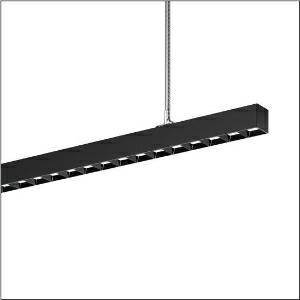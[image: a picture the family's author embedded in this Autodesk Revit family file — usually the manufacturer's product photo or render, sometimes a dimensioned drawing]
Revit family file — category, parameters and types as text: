
# Revit family: silica_21_51mx34dc4dbb
name_source: partatom
category: Lighting Fixtures
units: mm (PartAtom-declared; Revit-internal decimal feet)

## family parameters
Cut with Voids When Loaded = No
Host = Face
Light Source = No
Part Type = Normal
Room Calculation Point = No
Round Connector Dimension = Use Diameter
Shared = No

## types (1)
- --- (1 x LED, 19200 lm, 120.3 W, 4000K)
    Apparent Load = 120 VA
    CIE Flux Codes = 74 94 99 56 100
    Color Rendering = 80
    Color Temperature = 4000K
    Default Elevation = 1800 mm
    Description = Silica 21, office luminaire, primary light control with darklight reflector, of PMMA, black, light emission: direct/indirect distribution, primary light characteristic: asymmetric, installation type: suspended mounting, LED, rated luminous flux: 19.200lm, luminous efficacy: 160lm/W, light colour: 840, colour temperature: 4000K, control gear: DALI 2, with terminal, 3+2-pole, max. 2.5mm², mains connection: 220..240V, AC, 50/60Hz, rated input power: 120.3W, luminaire housing, of aluminium, matt jet black (RAL 9005), length: 3.004mm, width: 53mm, height: 53mm, protection rating (complete): IP20, insulation class (complete): insulation class I (protective earthing), certification: CE, permissible operating ambient temperature: 0..+35°C, standard: EN 50419, packaging unit: 1 piece
    Height = 53 mm
    Lamp = 1 x LED
    Lamp Light Flux = 19200 lm
    Lamp Power = 120.3 W
    Lamp count = 1
    Length = 3004 mm
    Luminous efficacy = 160 lm/W
    Manufacturer = Siteco
    ModVariant = No
    Model = 51MX34DC4DBB
    Mounting Place = Ceiling
    Mounting Type = Pendant
    Number of Poles = 1
    OnlyDefault = Yes
    Power Factor = 1
    Product Name = Silica 21
    Product group = office luminaire | ceiling pendant
    ProductGroupID = 903
    Protection Class = Protection class I
    Protection Degree = IP 20
    RLX_Detail_Level = 1
    RLX_Emergency_Light_Flux = 0 lm
    RLX_Emergency_Type = 0
    RLX_Emergency_Type_DB = No
    RlxData = <blob elided: 67433 chars, md5=6e270fa8>
    Socket = socket
    Standby Power = 0 W
    System Light Flux = 19200 lm
    System Power = 120 W
    Type Comments = factory setting: luminous flux: 100 % | dim-lin: 254 | 418 mA
    Type Image = l_1335852.jpg
    URL = http://relux.com
    VarID = @adj_120261
    Voltage = 0 V
    Weight = 0.00 kg
    Width = 53 mm

## geometry (parser evidence)
native form markers: Blend x4, Sweep x12
no freeform markers — native parametric forms only
